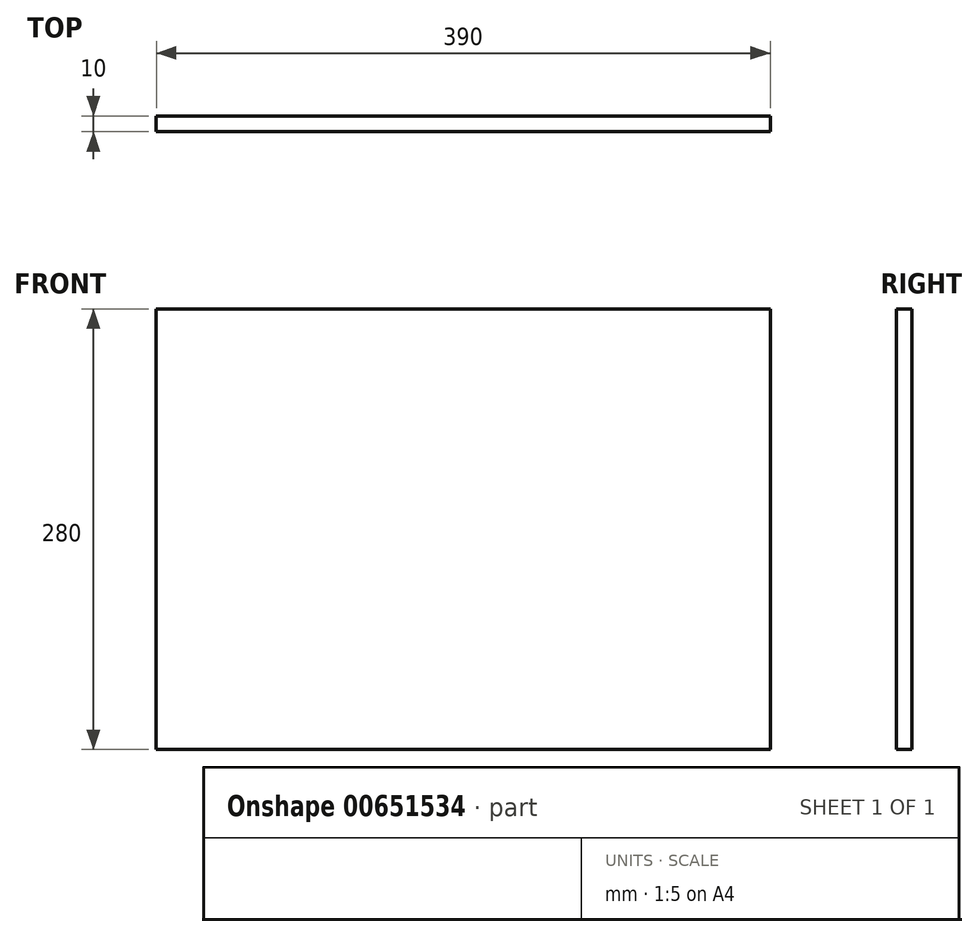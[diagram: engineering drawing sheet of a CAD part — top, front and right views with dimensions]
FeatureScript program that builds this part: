
annotation { "Feature Type Name" : "Feature", "Feature Type Description" : "" }
export const myFeature = defineFeature(function(context is Context, id is Id, definition is map)
    precondition{}
    {
        {
            assignVariable(context, id + "F0", {"name" : "d", "anyValue" : 10});
        }
        {
            var Q0;
            Q0=qCreatedBy(makeId("Front.planeOp"),FACE);
            var sketch = newSketch(context, id + "F1", { "sketchPlane" : qUnion([Q0])});
            skLineSegment(sketch, "E0.bottom", {"start": v(-211.36, 119.67) * mm, "end": v(178.64, 119.67) * mm});
            skLineSegment(sketch, "E0.top", {"start": v(-211.36, -160.33) * mm, "end": v(178.64, -160.33) * mm});
            skLineSegment(sketch, "E0.left", {"start": v(-211.36, 119.67) * mm, "end": v(-211.36, -160.33) * mm});
            skLineSegment(sketch, "E0.right", {"start": v(178.64, 119.67) * mm, "end": v(178.64, -160.33) * mm});
            skSolve(sketch);
        }
        {
            var Q0;
            Q0=makeQuery(id+"F1.imprint","IMPRINT",FACE,{"disambiguationData":[TD([[makeQuery(id+"F1.imprint","IMPRINT",EDGE,{"derivedFrom":sQuery(id+"F1.wireOp",EDGE,"E0.bottom")}),-1.0]])]});
            extrude(context, id + "F2", {"entities" : qUnion([Q0]), "depth" : (getVariable(context, 'd')) * mm, "offsetDistance" : 25 * mm});
        }
    });
